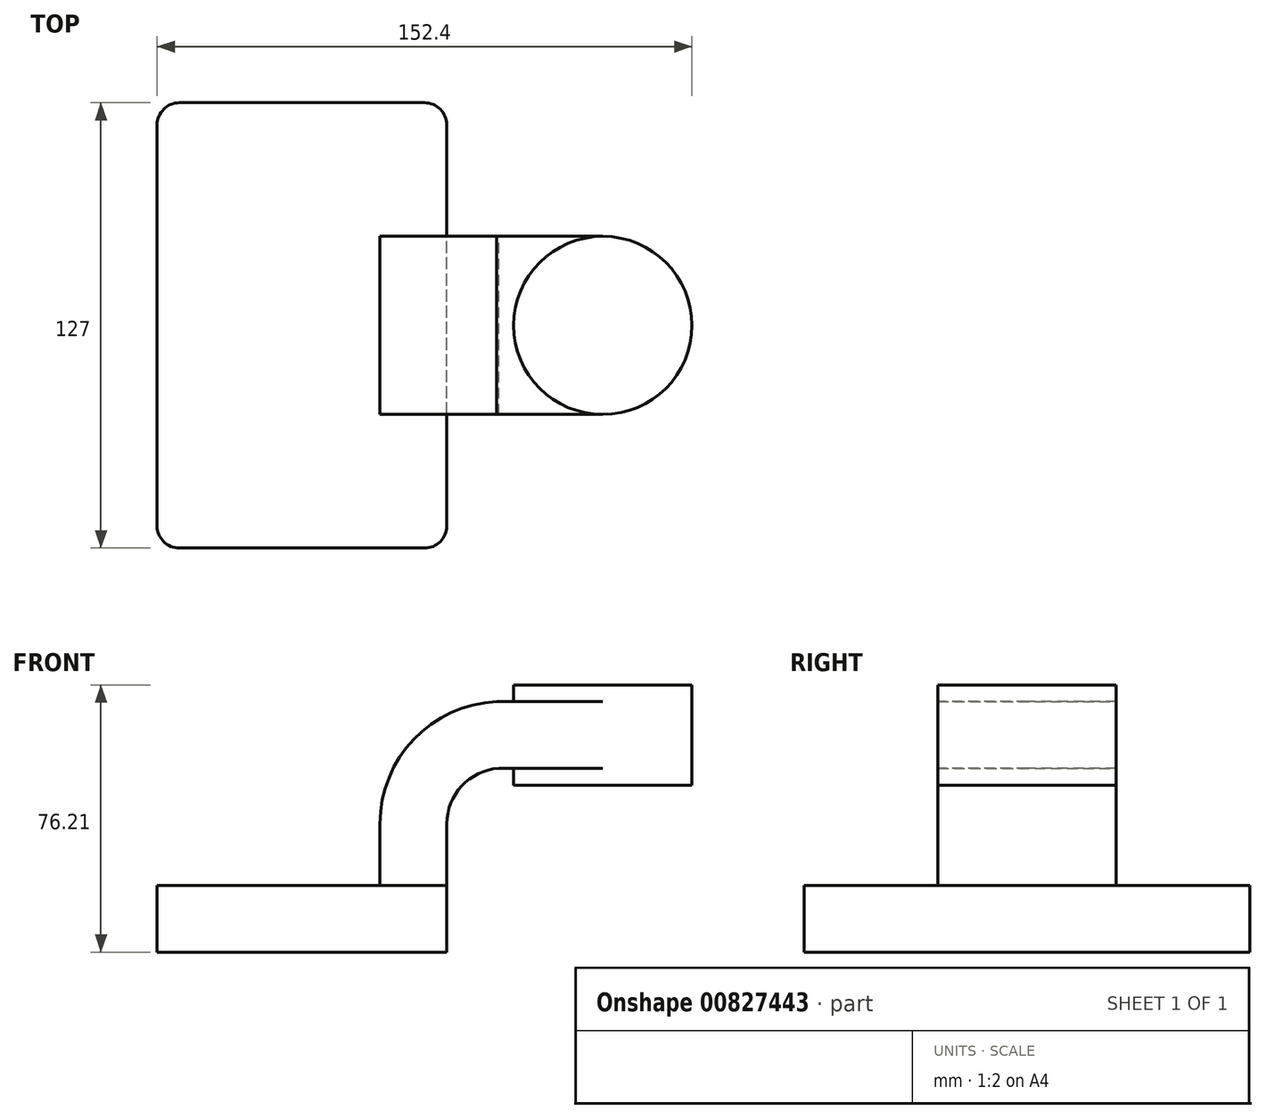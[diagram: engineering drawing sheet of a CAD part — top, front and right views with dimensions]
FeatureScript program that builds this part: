
annotation { "Feature Type Name" : "Feature", "Feature Type Description" : "" }
export const myFeature = defineFeature(function(context is Context, id is Id, definition is map)
    precondition{}
    {
        {
            var Q0;
            Q0=qCreatedBy(makeId("Front.planeOp"),FACE);
            var sketch = newSketch(context, id + "F0", { "sketchPlane" : qUnion([Q0])});
            skLineSegment(sketch, "E0.bottom", {"start": v(-41.28, -9.52) * mm, "end": v(41.28, -9.52) * mm});
            skLineSegment(sketch, "E0.top", {"start": v(-41.28, 9.53) * mm, "end": v(41.28, 9.53) * mm});
            skLineSegment(sketch, "E0.left", {"start": v(-41.27, -9.53) * mm, "end": v(-41.27, 9.52) * mm});
            skLineSegment(sketch, "E0.right", {"start": v(41.28, -9.53) * mm, "end": v(41.28, 9.52) * mm});
            skPoint(sketch, "E0.middle", {"position": v(0, 0) * mm});
            skLineSegment(sketch, "E1.bottom", {"start": v(60.33, 38.1) * mm, "end": v(111.12, 38.1) * mm});
            skLineSegment(sketch, "E1.top", {"start": v(60.33, 66.68) * mm, "end": v(111.12, 66.68) * mm});
            skLineSegment(sketch, "E1.left", {"start": v(60.33, 38.1) * mm, "end": v(60.33, 66.67) * mm});
            skLineSegment(sketch, "E1.right", {"start": v(111.12, 38.1) * mm, "end": v(111.12, 66.67) * mm});
            skPoint(sketch, "E1.middle", {"position": v(85.72, 52.39) * mm});
            skLineSegment(sketch, "E2", {"start": v(41.28, 9.52) * mm, "end": v(41.28, 27.04) * mm});
            skArc(sketch, "E3", {"start": v(41.28, 27.04) * mm, "mid": v(45.54, 37.87) * mm, "end": v(56.05, 42.88) * mm});
            skLineSegment(sketch, "E4", {"start": v(56.05, 42.88) * mm, "end": v(85.72, 42.88) * mm});
            skLineSegment(sketch, "E5.0", {"start": v(55.51, 61.93) * mm, "end": v(85.72, 61.93) * mm});
            skArc(sketch, "E5.1", {"start": v(22.23, 27.04) * mm, "mid": v(31.88, 51.15) * mm, "end": v(55.51, 61.93) * mm});
            skLineSegment(sketch, "E5.2", {"start": v(22.23, 9.53) * mm, "end": v(22.23, 27.04) * mm});
            skLineSegment(sketch, "E6", {"start": v(85.72, 38.1) * mm, "end": v(85.72, 66.67) * mm});
            skFitSpline(sketch, "E7", {"points": [v(-41.27, 9.53) * mm, v(55.51, 61.93) * mm], "startDerivative": vector(0, 120.3) * mm, "endDerivative": vector(206.42, 0) * mm});
            skSolve(sketch);
        }
        {
            var Q0;
            Q0=makeQuery(id+"F0.imprint","IMPRINT",FACE,{"disambiguationData":[TD([[makeQuery(id+"F0.imprint","IMPRINT",EDGE,{"derivedFrom":sQuery(id+"F0.wireOp",EDGE,"E0.bottom")}),1.0]])]});
            extrude(context, id + "F1", {"entities" : qUnion([Q0]), "endBound" : BoundingType.SYMMETRIC, "depth" : 127 * mm, "offsetDistance" : 25.4 * mm});
        }
        {
            var Q0;
            {var subQ1=sQuery(id+"F0.wireOp",EDGE,"E2");Q0=makeQuery(id+"F0.imprint","IMPRINT",FACE,{"disambiguationData":[TD([[makeQuery(id+"F0.imprint","IMPRINT",EDGE,{"derivedFrom":subQ1}),1.0]])]});}
            var Q1;
            {var subQ0=sQuery(id+"F0.wireOp",EDGE,"E4");var subQ1=sQuery(id+"F0.wireOp",EDGE,"E1.left");var subQ2=makeQuery(id+"F0.imprint","INTERSECT",VERTEX,{"derivedFrom":[subQ1,subQ0]});Q1=makeQuery(id+"F0.imprint","IMPRINT",FACE,{"disambiguationData":[TD([[makeQuery(id+"F0.imprint","IMPRINT",EDGE,{"disambiguationData":[TD([[subQ2,-1.0]])],"derivedFrom":subQ1}),-1.0]])]});}
            extrude(context, id + "F2", {"entities" : qUnion([Q0, Q1]), "endBound" : BoundingType.SYMMETRIC, "depth" : 50.8 * mm, "offsetDistance" : 25.4 * mm});
        }
        {
            var Q0;
            Q0=makeQuery(id+"F0.imprint","IMPRINT",FACE,{"disambiguationData":[TD([[makeQuery(id+"F0.imprint","IMPRINT",EDGE,{"derivedFrom":sQuery(id+"F0.wireOp",EDGE,"E5.1")}),1.0]])]});
            extrude(context, id + "F3", {"entities" : qUnion([Q0]), "endBound" : BoundingType.SYMMETRIC, "depth" : 15.88 * mm, "offsetDistance" : 25.4 * mm});
        }
        {
            var Q0;
            {var subQ0=sQuery(id+"F0.wireOp",EDGE,"E1.right");Q0=makeQuery(id+"F0.imprint","IMPRINT",FACE,{"disambiguationData":[TD([[makeQuery(id+"F0.imprint","IMPRINT",EDGE,{"derivedFrom":subQ0}),1.0]])]});}
            var Q1;
            Q1=sQuery(id+"F0.wireOp",EDGE,"E6");
            revolve(context, id + "F4", {"operationType" : NewBodyOperationType.ADD, "surfaceOperationType" : NewSurfaceOperationType.NEW, "entities" : qUnion([Q0]), "axis" : qUnion([Q1]), "revolveType" : RevolveType.FULL});
        }
        {
            var Q0;
            Q0=makeQuery(id+"F1.opExtrude","CAP_EDGE",EDGE,{"disambiguationData":[OSD([sQuery(id+"F0.wireOp",EDGE,"E0.right")])],"isStart":false});
            var Q1;
            Q1=makeQuery(id+"F1.opExtrude","CAP_EDGE",EDGE,{"disambiguationData":[OSD([sQuery(id+"F0.wireOp",EDGE,"E0.right")])],"isStart":true});
            var Q2;
            Q2=makeQuery(id+"F1.opExtrude","CAP_EDGE",EDGE,{"disambiguationData":[OSD([sQuery(id+"F0.wireOp",EDGE,"E0.left")])],"isStart":true});
            var Q3;
            Q3=makeQuery(id+"F1.opExtrude","CAP_EDGE",EDGE,{"disambiguationData":[OSD([sQuery(id+"F0.wireOp",EDGE,"E0.left")])],"isStart":false});
            fillet(context, id + "F5", {"entities" : qUnion([Q0, Q1, Q2, Q3]), "radius" : 6.35 * mm, "tangentPropagation" : true, "allowEdgeOverflow" : false});
        }
    });
